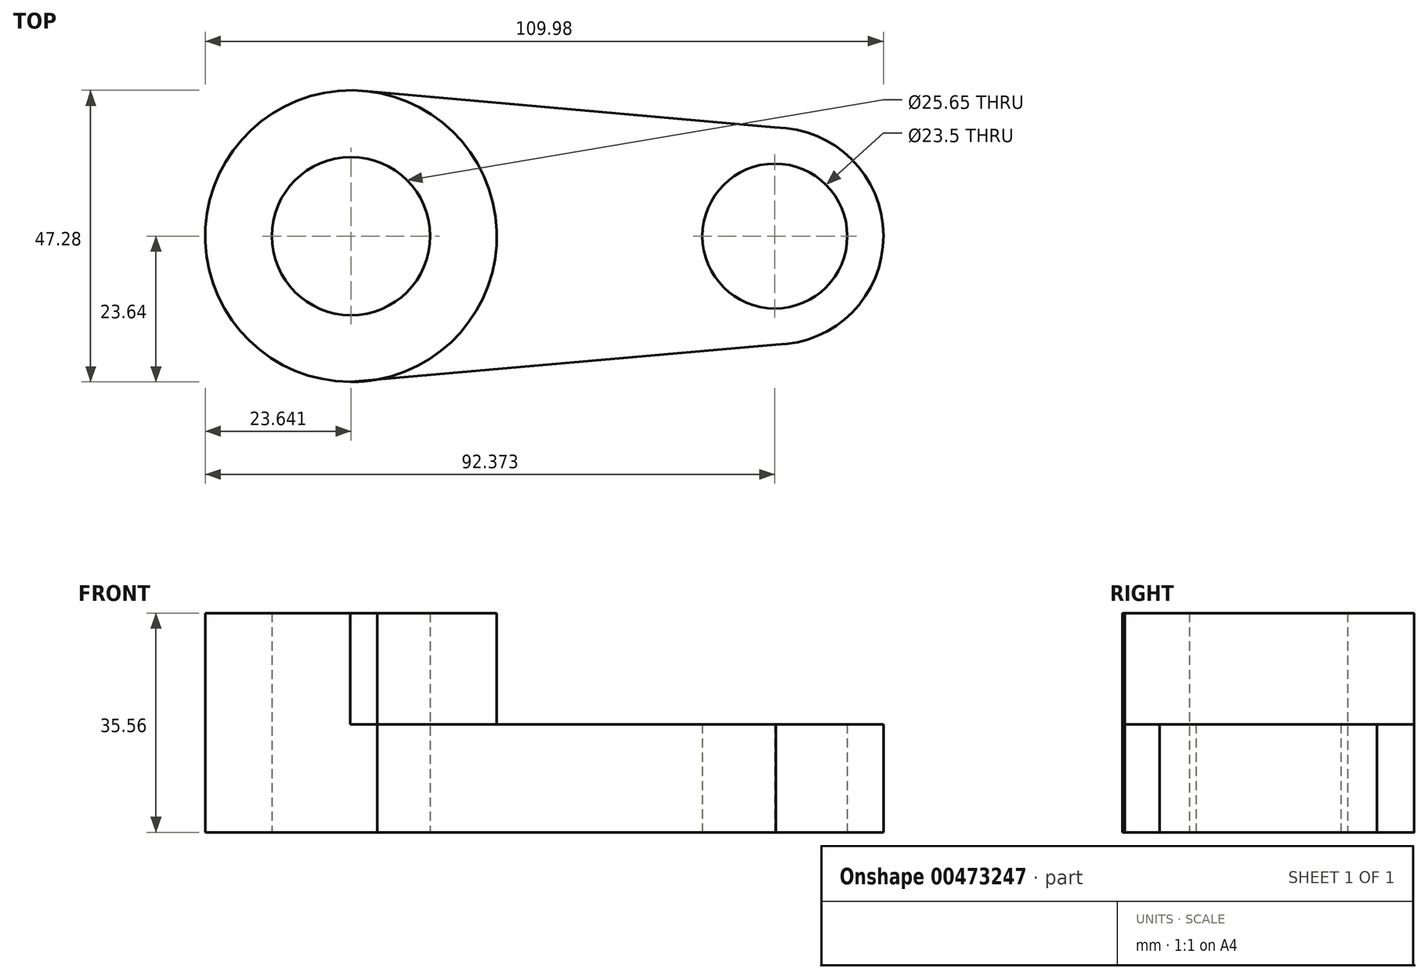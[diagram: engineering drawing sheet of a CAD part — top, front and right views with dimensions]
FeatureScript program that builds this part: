
annotation { "Feature Type Name" : "Feature", "Feature Type Description" : "" }
export const myFeature = defineFeature(function(context is Context, id is Id, definition is map)
    precondition{}
    {
        {
            var Q0;
            Q0=qCreatedBy(makeId("Top.planeOp"),FACE);
            var sketch = newSketch(context, id + "F0", { "sketchPlane" : qUnion([Q0])});
            skCircle(sketch, "E0", {"center": v(-39.59, 0) * mm, "radius": 23.64 * mm});
            skCircle(sketch, "E1", {"center": v(-39.59, 0) * mm, "radius": 12.82 * mm});
            skCircle(sketch, "E2", {"center": v(29.14, 0) * mm, "radius": 11.75 * mm});
            skArc(sketch, "E3", {"start": v(29.3, -17.61) * mm, "mid": v(46.75, 0.08) * mm, "end": v(29.14, 17.61) * mm});
            skLineSegment(sketch, "E4", {"start": v(29.14, 17.61) * mm, "end": v(-37.5, 23.55) * mm});
            skLineSegment(sketch, "E5", {"start": v(29.3, -17.61) * mm, "end": v(-39.74, -23.64) * mm});
            skSolve(sketch);
        }
        {
            var Q0;
            Q0=makeQuery(id+"F0.imprint","IMPRINT",FACE,{"disambiguationData":[TD([[makeQuery(id+"F0.imprint","IMPRINT",EDGE,{"derivedFrom":sQuery(id+"F0.wireOp",EDGE,"E1")}),-1.0]])]});
            extrude(context, id + "F1", {"entities" : qUnion([Q0]), "depth" : 35.56 * mm});
        }
        {
            var Q0;
            Q0=qSketchRegion(id+"F0",true);
            extrude(context, id + "F2", {"entities" : qUnion([Q0]), "operationType" : NewBodyOperationType.ADD, "depth" : 17.53 * mm});
        }
    });
